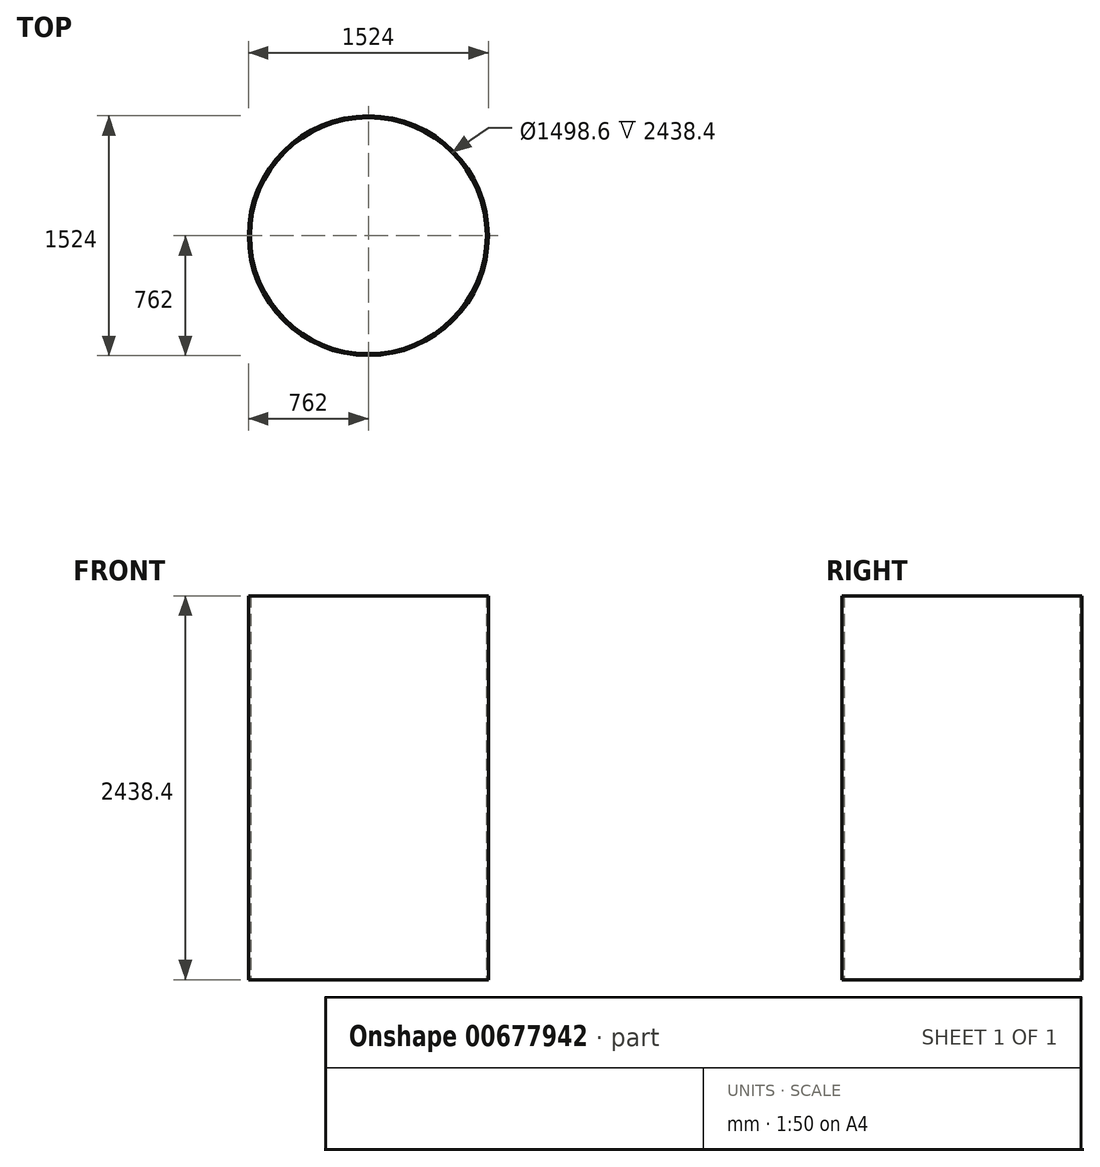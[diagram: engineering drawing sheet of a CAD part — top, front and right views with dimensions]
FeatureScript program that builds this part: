
annotation { "Feature Type Name" : "Feature", "Feature Type Description" : "" }
export const myFeature = defineFeature(function(context is Context, id is Id, definition is map)
    precondition{}
    {
        {
            var Q0;
            Q0=qCreatedBy(makeId("Top.planeOp"),FACE);
            var sketch = newSketch(context, id + "F0", { "sketchPlane" : qUnion([Q0])});
            skCircle(sketch, "E0", {"center": v(0, 0) * mm, "radius": 762 * mm});
            skCircle(sketch, "E1", {"center": v(0, 0) * mm, "radius": 749.3 * mm});
            skSolve(sketch);
        }
        {
            var Q0;
            Q0 = qSketchRegion(id + "F0", true);
            extrude(context, id + "F1", {"entities" : qUnion([Q0]), "depth" : 2438.4 * mm, "offsetDistance" : 25.4 * mm});
        }
    });
